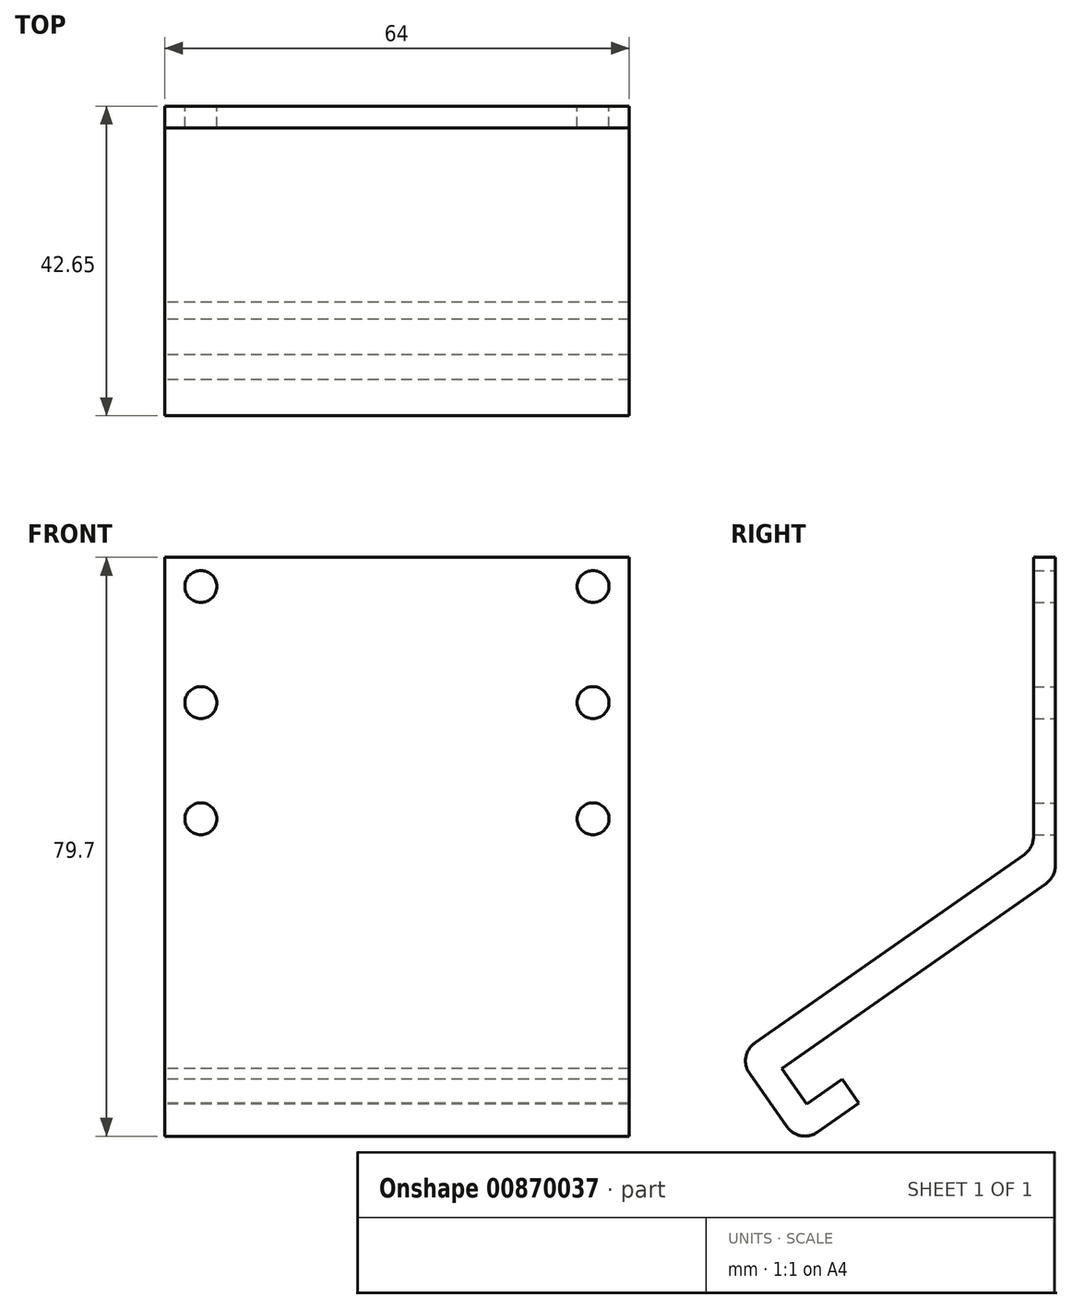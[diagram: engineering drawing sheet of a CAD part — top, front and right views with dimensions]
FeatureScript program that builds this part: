
annotation { "Feature Type Name" : "Feature", "Feature Type Description" : "" }
export const myFeature = defineFeature(function(context is Context, id is Id, definition is map)
    precondition{}
    {
        {
            var Q0;
            Q0=qCreatedBy(makeId("Front.planeOp"),FACE);
            var sketch = newSketch(context, id + "F0", { "sketchPlane" : qUnion([Q0])});
            skLineSegment(sketch, "E0.bottom", {"start": v(32, -20) * mm, "end": v(-32, -20) * mm});
            skLineSegment(sketch, "E0.top", {"start": v(32, 20) * mm, "end": v(-32, 20) * mm});
            skLineSegment(sketch, "E0.left", {"start": v(32, -20) * mm, "end": v(32, 20) * mm});
            skLineSegment(sketch, "E0.right", {"start": v(-32, -20) * mm, "end": v(-32, 20) * mm});
            skPoint(sketch, "E0.middle", {"position": v(0, 0) * mm});
            skCircle(sketch, "E1", {"center": v(-27, 0) * mm, "radius": 2.2 * mm});
            skLineSegment(sketch, "E2", {"start": v(-27, -20) * mm, "end": v(-27, 20) * mm, "construction": true});
            skCircle(sketch, "E3", {"center": v(-27, 16) * mm, "radius": 2.2 * mm});
            skCircle(sketch, "E4.MirrorC", {"center": v(-27, -16) * mm, "radius": 2.2 * mm});
            skCircle(sketch, "E5.MirrorC", {"center": v(27, 16) * mm, "radius": 2.2 * mm});
            skCircle(sketch, "E6.MirrorC", {"center": v(27, 0) * mm, "radius": 2.2 * mm});
            skCircle(sketch, "E7.MirrorC", {"center": v(27, -16) * mm, "radius": 2.2 * mm});
            skLineSegment(sketch, "E8.bottom", {"start": v(-32, -20) * mm, "end": v(32, -20) * mm});
            skSolve(sketch);
        }
        {
            var Q0;
            Q0=qSketchRegion(id+"F0",true);
            extrude(context, id + "F1", {"entities" : qUnion([Q0]), "depth" : 3 * mm, "offsetDistance" : 25 * mm});
        }
        {
            var Q0;
            Q0=qCreatedBy(makeId("Right.planeOp"),FACE);
            var sketch = newSketch(context, id + "F2", { "sketchPlane" : qUnion([Q0])});
            skLineSegment(sketch, "E9", {"start": v(-3, -20) * mm, "end": v(-43.83, -48.59) * mm});
            skLineSegment(sketch, "E10", {"start": v(-43.83, -48.59) * mm, "end": v(-40.96, -52.68) * mm});
            skLineSegment(sketch, "E11", {"start": v(-40.96, -52.68) * mm, "end": v(0, -24) * mm});
            skLineSegment(sketch, "E12", {"start": v(0, -24) * mm, "end": v(0, -20) * mm});
            skLineSegment(sketch, "E13", {"start": v(-3, -20) * mm, "end": v(0, -20) * mm});
            skLineSegment(sketch, "E14", {"start": v(-40.96, -52.68) * mm, "end": v(-35.22, -60.87) * mm});
            skLineSegment(sketch, "E15", {"start": v(-35.22, -60.87) * mm, "end": v(-27.03, -55.14) * mm});
            skLineSegment(sketch, "E16", {"start": v(-27.03, -55.14) * mm, "end": v(-29.32, -51.86) * mm});
            skLineSegment(sketch, "E17", {"start": v(-29.32, -51.86) * mm, "end": v(-34.24, -55.3) * mm});
            skLineSegment(sketch, "E18", {"start": v(-34.24, -55.3) * mm, "end": v(-37.68, -50.39) * mm});
            skSolve(sketch);
        }
        {
            var Q0;
            Q0 = qSketchRegion(id + "F2", true);
            extrude(context, id + "F3", {"entities" : qUnion([Q0]), "operationType" : NewBodyOperationType.ADD, "endBound" : BoundingType.SYMMETRIC, "depth" : 64 * mm, "offsetDistance" : 25 * mm});
        }
        {
            var Q0;
            Q0=makeQuery(id+"F3.boolean.opBoolean","MERGE",EDGE,{"derivedFrom":[makeQuery(id+"F1.opExtrude","CAP_EDGE",EDGE,{"disambiguationData":[OSD([sQuery(id+"F0.wireOp",EDGE,"E8.top"),sQuery(id+"F0.wireOp",EDGE,"KLS2BBdy-9Qtb-1H7o-hbpf-MN1BBosknPLz.top"),sQuery(id+"F0.wireOp",EDGE,"pcLGZwba-Mvlo-nCCo-qlRg-PAg5c1R6vDbR.top")])],"isStart":false}),makeQuery(id+"F3.opExtrude","SWEPT_EDGE",EDGE,{"disambiguationData":[OSD([sQuery(id+"F2.wireOp",EDGE,"E9"),sQuery(id+"F2.wireOp",EDGE,"E13")])]})]});
            var Q1;
            Q1=makeQuery(id+"F3.opExtrude","SWEPT_EDGE",EDGE,{"disambiguationData":[OSD([sQuery(id+"F2.wireOp",EDGE,"E11"),sQuery(id+"F2.wireOp",EDGE,"E12")])]});
            var Q2;
            Q2=makeQuery(id+"F3.opExtrude","SWEPT_EDGE",EDGE,{"disambiguationData":[OSD([sQuery(id+"F2.wireOp",EDGE,"E9"),sQuery(id+"F2.wireOp",EDGE,"E10")])]});
            var Q3;
            Q3=makeQuery(id+"F3.opExtrude","SWEPT_EDGE",EDGE,{"disambiguationData":[OSD([sQuery(id+"F2.wireOp",EDGE,"E14"),sQuery(id+"F2.wireOp",EDGE,"E15")])]});
            fillet(context, id + "F4", {"entities" : qUnion([Q0, Q1, Q2, Q3]), "radius" : 3 * mm, "tangentPropagation" : true, "allowEdgeOverflow" : false});
        }
    });
